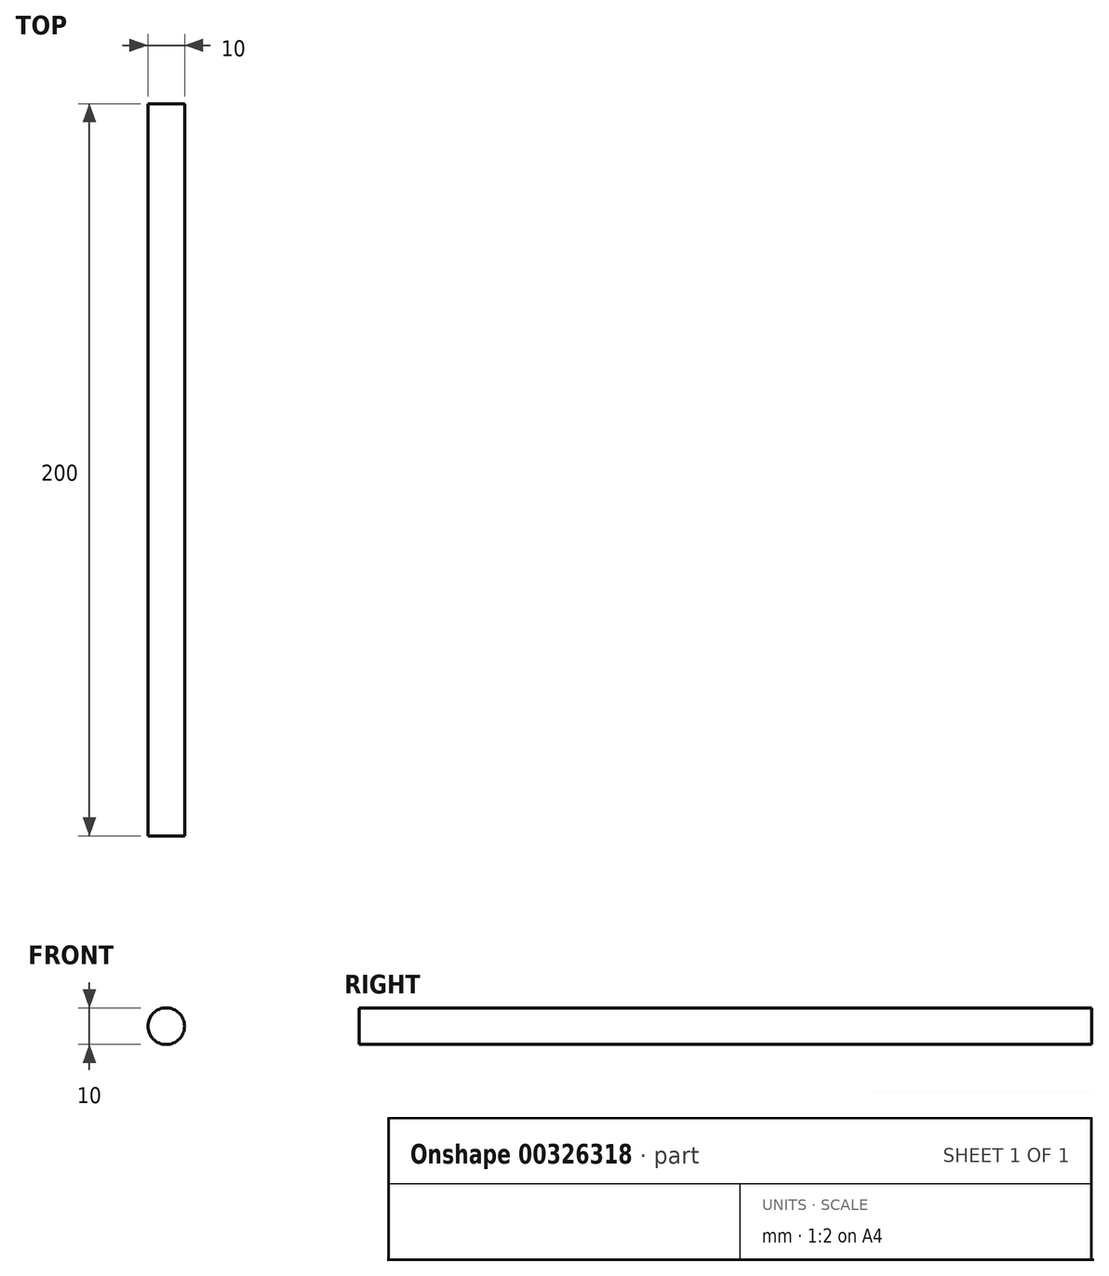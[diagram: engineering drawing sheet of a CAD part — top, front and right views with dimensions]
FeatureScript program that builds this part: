
annotation { "Feature Type Name" : "Feature", "Feature Type Description" : "" }
export const myFeature = defineFeature(function(context is Context, id is Id, definition is map)
    precondition{}
    {
        {
            var Q0;
            Q0=qCreatedBy(makeId("Front.planeOp"),FACE);
            var sketch = newSketch(context, id + "F0", { "sketchPlane" : qUnion([Q0])});
            skCircle(sketch, "E0", {"center": v(-36.04, 38.2) * mm, "radius": 5 * mm});
            skSolve(sketch);
        }
        {
            var Q0;
            Q0=makeQuery(id+"F0.imprint","IMPRINT",FACE,{"disambiguationData":[TD([[makeQuery(id+"F0.imprint","IMPRINT",EDGE,{"derivedFrom":sQuery(id+"F0.wireOp",EDGE,"E0")}),1.0]])]});
            extrude(context, id + "F1", {"entities" : qUnion([Q0]), "depth" : 200 * mm});
        }
    });
